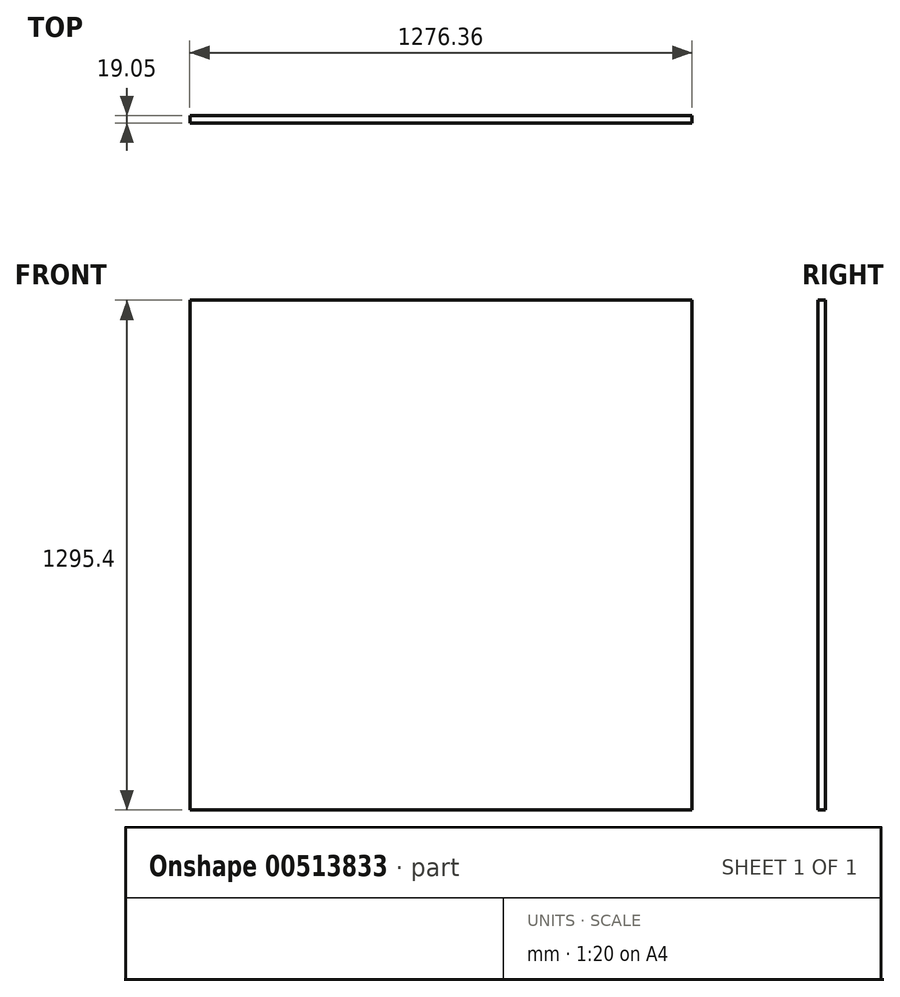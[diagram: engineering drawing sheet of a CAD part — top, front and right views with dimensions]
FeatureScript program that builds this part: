
annotation { "Feature Type Name" : "Feature", "Feature Type Description" : "" }
export const myFeature = defineFeature(function(context is Context, id is Id, definition is map)
    precondition{}
    {
        {
            var Q0;
            Q0=qCreatedBy(makeId("Front.planeOp"),FACE);
            var sketch = newSketch(context, id + "F0", { "sketchPlane" : qUnion([Q0])});
            skLineSegment(sketch, "E0.bottom", {"start": v(638.17, 647.7) * mm, "end": v(-638.18, 647.7) * mm});
            skLineSegment(sketch, "E0.top", {"start": v(638.18, -647.7) * mm, "end": v(-638.17, -647.7) * mm});
            skLineSegment(sketch, "E0.left", {"start": v(638.17, 647.7) * mm, "end": v(638.18, -647.7) * mm});
            skLineSegment(sketch, "E0.right", {"start": v(-638.18, 647.7) * mm, "end": v(-638.17, -647.7) * mm});
            skPoint(sketch, "E0.middle", {"position": v(0, 0) * mm});
            skSolve(sketch);
        }
        {
            var Q0;
            Q0 = qSketchRegion(id + "F0", true);
            extrude(context, id + "F1", {"entities" : qUnion([Q0]), "depth" : 19.05 * mm});
        }
    });
